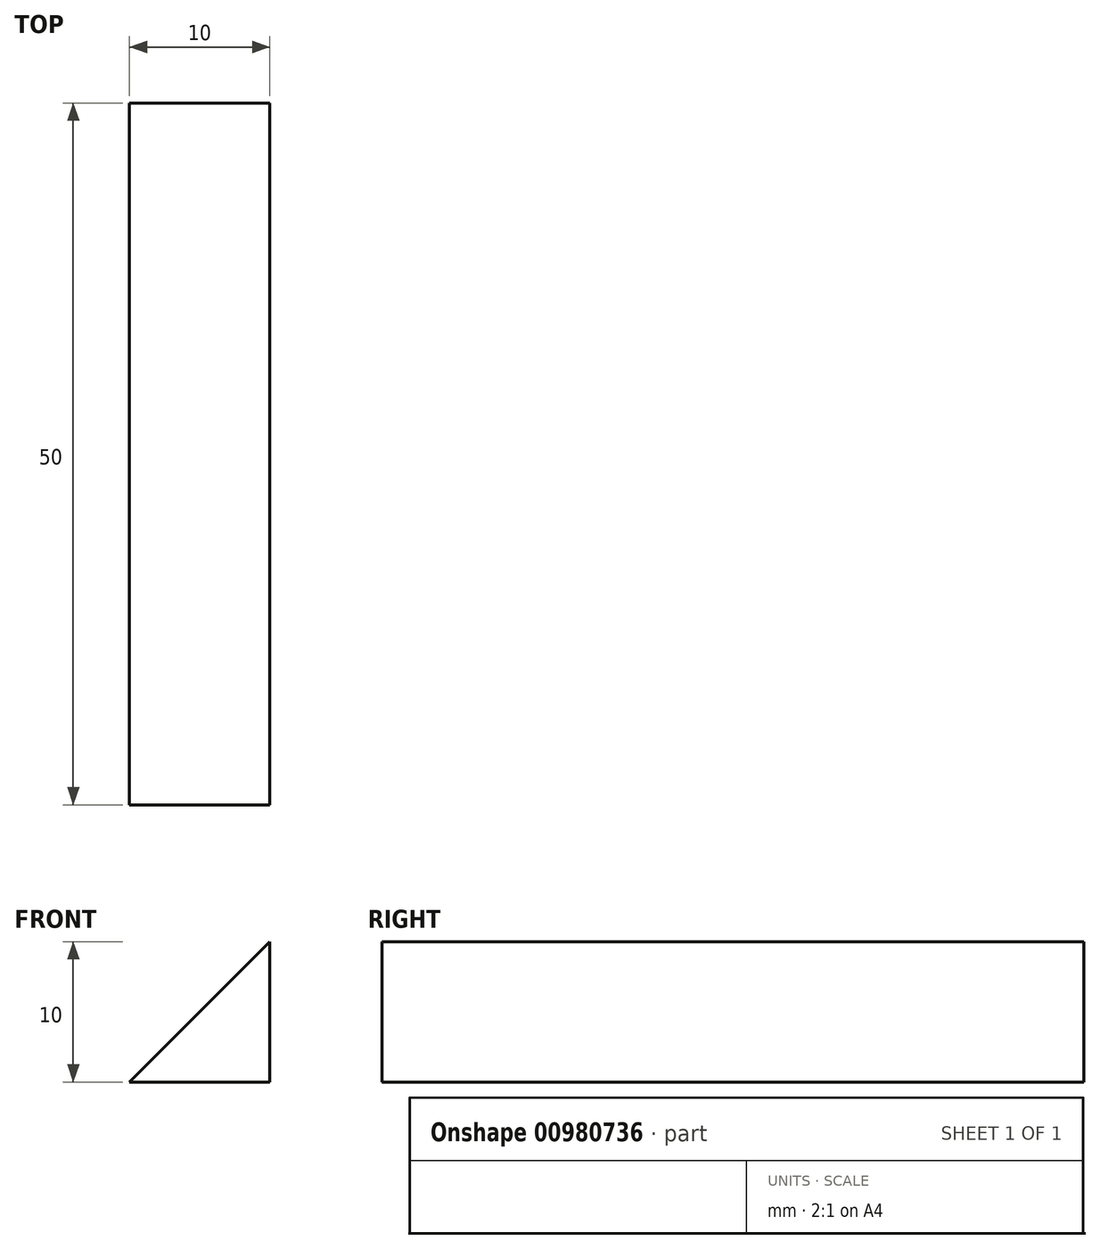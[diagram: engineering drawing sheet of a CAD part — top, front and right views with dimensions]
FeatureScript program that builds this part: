
annotation { "Feature Type Name" : "Feature", "Feature Type Description" : "" }
export const myFeature = defineFeature(function(context is Context, id is Id, definition is map)
    precondition{}
    {
        {
            var Q0;
            Q0=qCreatedBy(makeId("Front.planeOp"),FACE);
            var sketch = newSketch(context, id + "F0", { "sketchPlane" : qUnion([Q0])});
            skLineSegment(sketch, "E0", {"start": v(0, 0) * mm, "end": v(0, 10) * mm});
            skLineSegment(sketch, "E1", {"start": v(0, 10) * mm, "end": v(-10, 0) * mm});
            skLineSegment(sketch, "E2", {"start": v(-10, 0) * mm, "end": v(0, 0) * mm});
            skSolve(sketch);
        }
        {
            var Q0;
            Q0 = qSketchRegion(id + "F0", true);
            extrude(context, id + "F1", {"entities" : qUnion([Q0]), "depth" : 50 * mm, "offsetDistance" : 25.4 * mm});
        }
    });
